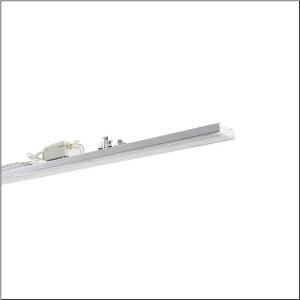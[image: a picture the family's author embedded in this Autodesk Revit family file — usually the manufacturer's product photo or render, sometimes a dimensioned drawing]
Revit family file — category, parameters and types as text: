
# Revit family: licross_r__21_recessed_mo_52tl14dn49xg_3f36
name_source: partatom
category: Lighting Fixtures
units: mm (PartAtom-declared; Revit-internal decimal feet)

## family parameters
Cut with Voids When Loaded = No
Host = Face
Light Source = No
Part Type = Normal
Room Calculation Point = No
Round Connector Dimension = Use Diameter
Shared = No

## types (1)
- --- (1 x LED, 9470 lm, 58 W, 4000K)
    Apparent Load = 58 VA
    CIE Flux Codes = 56 84 97 100 100
    Color Rendering = 80
    Color Temperature = 4000K
    Default Elevation = 1800 mm
    Description = Licross® 21 Recessed MO, luminaire insert, of sheet steel, galvanised, coil coated, white, length: 1.500mm, width: 66mm, height: 67mm, LED rated luminous flux: 9.470lm, light colour: 840, control gear: DALI 2, with plug, 5-pole, with phase selection, mains connection: 220..240V, AC, 50/60Hz, rated input power: 58W, halogen-free wiring, primary light control with lens, of plastic, primary optical cover: cover, of PMMA, light emission: direct distribution, primary light characteristic: asymmetric, protection rating (complete): IP40, insulation class (complete): insulation class I (protective earthing), certification: CE, ENEC, VDE, UKCA, protection symbol: D if used in an environment without relevant dust loads with corresponding accessories, impact resistance: IK06, permissible ambient temperature for indoor applications: -25..+35°C, corresponds to IFS (International Featured Standards) requirements for safety and quality in the food industry, reducing of maximum allowable ambient temperature of 5°C with ceiling mounting, LABS conformity tested according to VDMA 24364:2018-05, packaging unit: 1 piece
    Height = 58 mm
    Lamp = 1 x LED
    Lamp Light Flux = 9470 lm
    Lamp Power = 58 W
    Lamp count = 1
    Length = 1500 mm
    Luminous efficacy = 163 lm/W
    Manufacturer = Siteco
    ModVariant = No
    Model = 52TL14DN49XG
    Mounting Place = Ceiling
    Mounting Type = Pendant
    Number of Poles = 1
    OnlyDefault = Yes
    Power Factor = 1
    Product Name = Licross® 21 Recessed MO
    Product group = luminaire insert
    ProductGroupID = 901
    Protection Class = Protection class I
    Protection Degree = IP 40
    RLX_Detail_Level = 1
    RLX_Emergency_Light_Flux = 0 lm
    RLX_Emergency_Type = 0
    RLX_Emergency_Type_DB = No
    RlxData = <blob elided: 25037 chars, md5=173cea81>
    Socket = socket
    Standby Power = 0 W
    System Light Flux = 9470 lm
    System Power = 58 W
    Type Comments = factory setting: luminous flux: 100 % | dim-lin: 254 | 390 mA
    Type Image = l_1296930.jpg
    URL = http://relux.com
    VarID = @adj_059369
    Voltage = 0 V
    Weight = 0.00 kg
    Width = 66 mm

## geometry (parser evidence)
native form markers: Blend x4, Sweep x9
no freeform markers — native parametric forms only
